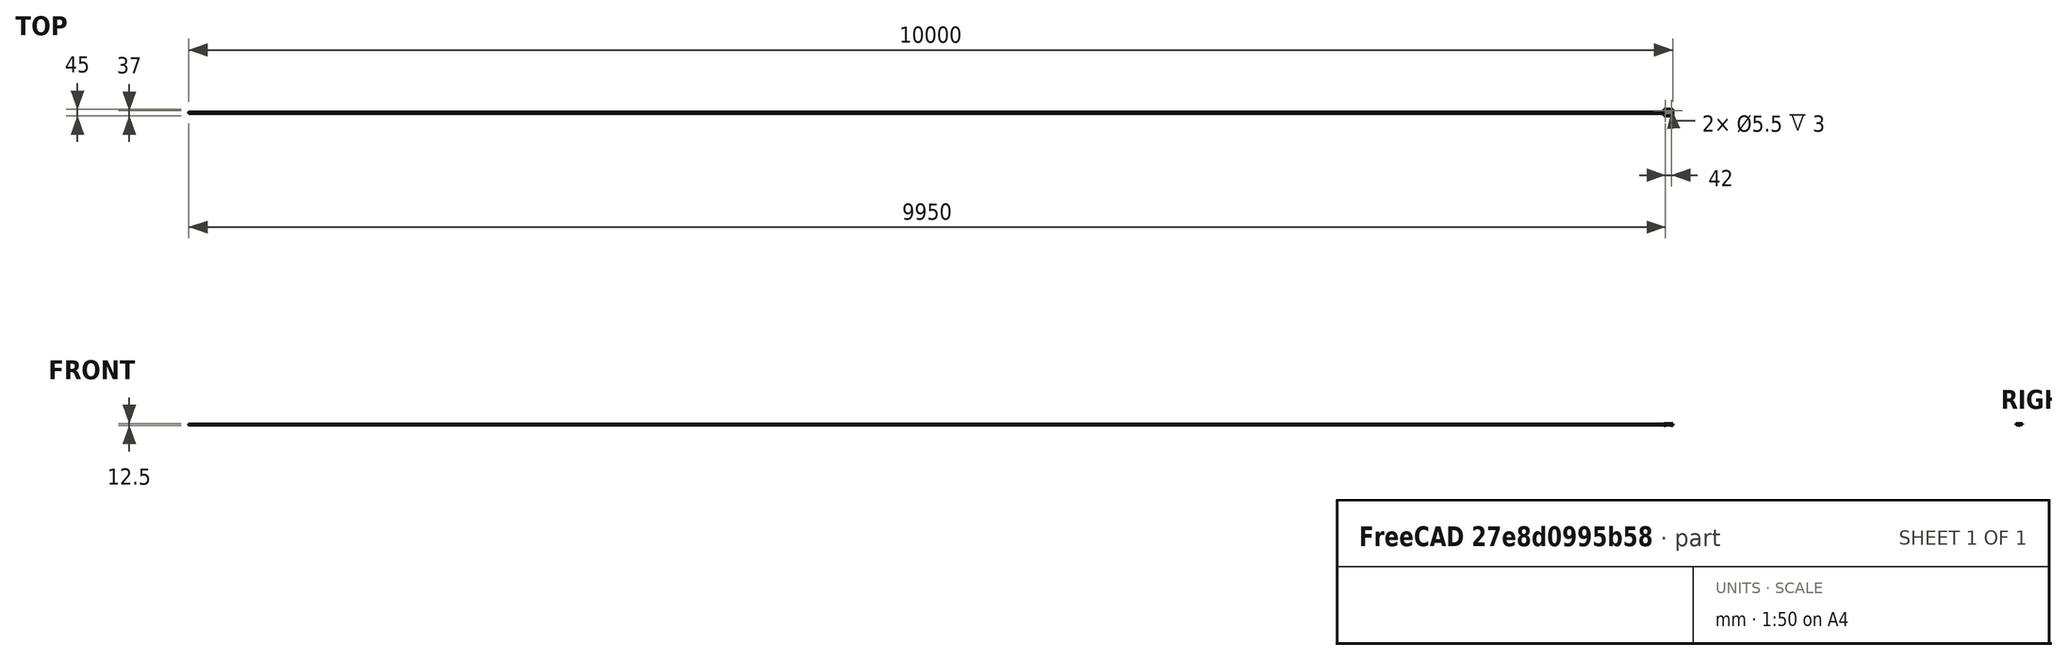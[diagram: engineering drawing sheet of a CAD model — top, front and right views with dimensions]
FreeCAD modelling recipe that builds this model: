
FCSTD DOCUMENT  (FreeCAD 0.16R)
Label: 60mmPed
License: All rights reserved
LicenseURL: http://en.wikipedia.org/wiki/All_rights_reserved
objects: Sketcher::SketchObject×6, PartDesign::Pocket×4, PartDesign::Pad×2, PartDesign::Fillet×1, Mesh::Feature×1
note: 19 computed .brp shape members not serialized (recipe doc carries the construction recipe); baked Part::Feature solids carry a one-line shape summary decoded from their .brp

FEATURE [Sketcher::SketchObject] Sketch
  sketch-geometry (4):
    g0: LineSegment StartX=0 StartY=-22.5 StartZ=0 EndX=0 EndY=22.5 EndZ=0
    g1: LineSegment StartX=0 StartY=22.5 StartZ=0 EndX=-60 EndY=22.5 EndZ=0
    g2: LineSegment StartX=0 StartY=-22.5 StartZ=0 EndX=-60 EndY=-22.5 EndZ=0
    g3: LineSegment StartX=-60 StartY=22.5 StartZ=0 EndX=-60 EndY=-22.5 EndZ=0
  constraints (11):
    c: Coincident(g0,g1)
    c: Horizontal(g1)
    c: Coincident(g2,g0)
    c: Horizontal(g2)
    c: Symmetric(g0,g0,g-1)
    c: PointOnObject(g-1,g0)
    c: Distance(g1) = 60
    c: Equal(g2,g1)
    c: Coincident(g1,g3)
    c: Coincident(g3,g2)
    c: Distance(g0) = 45
FEATURE [PartDesign::Pad] Pad
  Length = 7
  Length2 = 100
  Sketch = -> Sketch
  Type = 0
FEATURE [Sketcher::SketchObject] Sketch001
  Placement = pos=(0,0,0) rot=(0.57735,0.57735,0.57735;2.0944rad)
  Support = -> Pad [Face1]
  sketch-geometry (1):
    g0: Circle CenterX=0 CenterY=0 CenterZ=0 NormalX=0 NormalY=0 NormalZ=1 Radius=5.5
  constraints (2):
    c: Coincident(g0,g-1)
    c: Radius(g0) = 5.5
FEATURE [PartDesign::Pocket] Pocket
  Length = 12
  Sketch = -> Sketch001
  Type = 0
FEATURE [Sketcher::SketchObject] Sketch002
  Placement = pos=(0,0,0) rot=(0.57735,0.57735,0.57735;2.0944rad)
  Support = -> Pocket [Face1]
  sketch-geometry (1):
    g0: Circle CenterX=0 CenterY=0 CenterZ=0 NormalX=0 NormalY=0 NormalZ=1 Radius=4.25
  constraints (2):
    c: Radius(g0) = 4.25
    c: Coincident(g0,g-1)
FEATURE [PartDesign::Pocket] Pocket001
  Length = 50
  Sketch = -> Sketch002
  Type = 1
FEATURE [Sketcher::SketchObject] Sketch003
  Placement = pos=(-58,0,0) rot=(0.57735,-0.57735,-0.57735;2.0944rad)
  Support = -> Pocket001 [Face9]
  sketch-geometry (1):
    g0: Circle CenterX=0 CenterY=0 CenterZ=0 NormalX=0 NormalY=0 NormalZ=1 Radius=5.5
  constraints (2):
    c: Coincident(g0,g-1)
    c: Radius(g0) = 5.5
FEATURE [PartDesign::Pocket] Pocket002
  Length = 12
  Sketch = -> Sketch003
  Type = 0
FEATURE [Sketcher::SketchObject] Sketch004
  ExternalGeometry = -> [Pocket002]
  Placement = pos=(0,0,0) rot=(1,0,0;3.14159rad)
  Support = -> Pocket002 [Face4]
  sketch-geometry (2):
    g0: Circle CenterX=-8 CenterY=14.5 CenterZ=0 NormalX=0 NormalY=0 NormalZ=1 Radius=2.5
    g1: Circle CenterX=-50 CenterY=14.5 CenterZ=0 NormalX=0 NormalY=0 NormalZ=1 Radius=2.5
  constraints (6):
    c: Radius(g0) = 2.5
    c: Equal(g0,g1)
    c: Distance(g0,g-3) = 8
    c: Distance(g0,g-5) = 8
    c: Distance(g1,g-3) = 8
    c: Distance(g1,g-4) = 8
FEATURE [PartDesign::Pad] Pad001
  Length = 2
  Length2 = 100
  Sketch = -> Sketch004
  Type = 0
FEATURE [Sketcher::SketchObject] Sketch005
  ExternalGeometry = -> [Pad001]
  Placement = pos=(0,0,0) rot=(1,0,0;3.14159rad)
  Support = -> Pad001 [Face4]
  sketch-geometry (2):
    g0: Circle CenterX=-8 CenterY=-14.5 CenterZ=0 NormalX=0 NormalY=0 NormalZ=1 Radius=2.75
    g1: Circle CenterX=-50 CenterY=-14.5 CenterZ=0 NormalX=0 NormalY=0 NormalZ=1 Radius=2.75
  constraints (6):
    c: Radius(g1) = 2.75
    c: Equal(g1,g0)
    c: DistanceX(g-2,g0) = -8
    c: Distance(g1,g-3) = 8
    c: Distance(g1,g-4) = 8
    c: Distance(g0,g-4) = 8
FEATURE [PartDesign::Pocket] Pocket003
  Length = 3
  Sketch = -> Sketch005
  Type = 0
FEATURE [PartDesign::Fillet] Fillet
  Base = -> Pocket003 [Edge26,Edge30,Edge6,Edge4]
  Radius = 15
FEATURE [Mesh::Feature] Mesh  label="Fillet (Meshed)"
